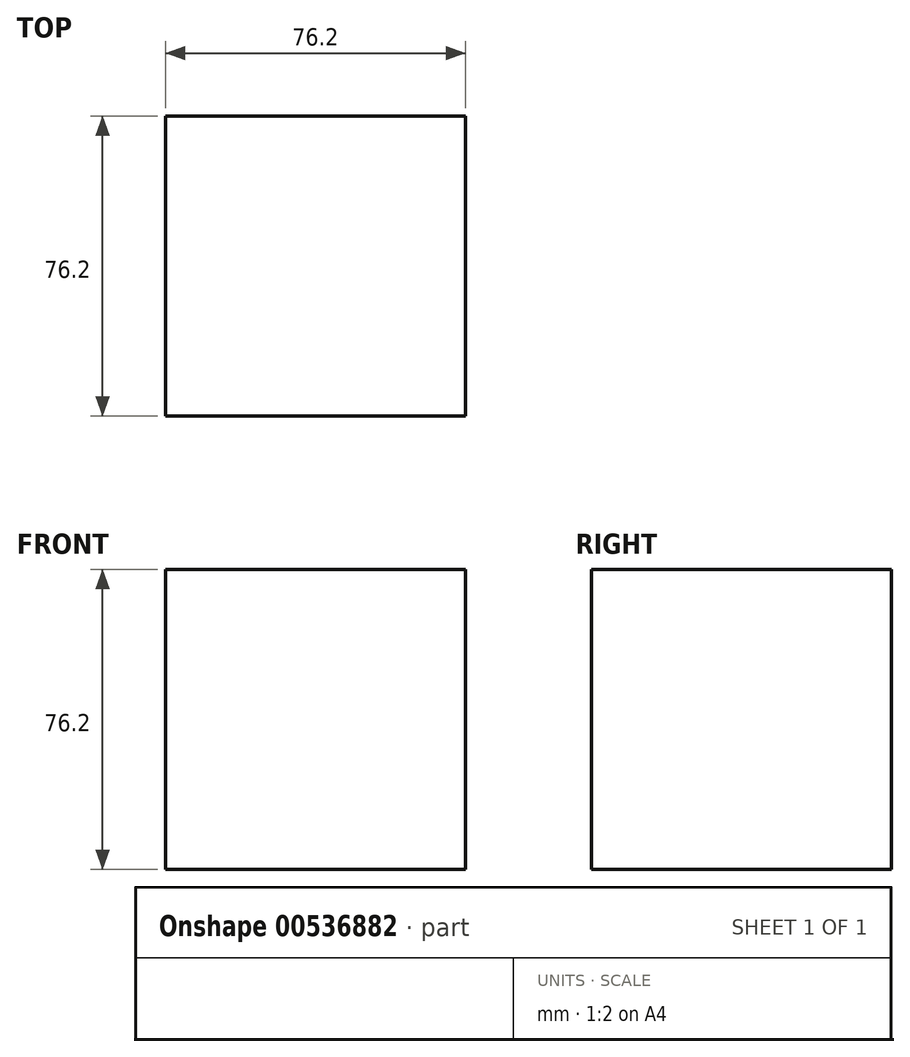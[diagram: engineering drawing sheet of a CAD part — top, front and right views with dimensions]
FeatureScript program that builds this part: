
annotation { "Feature Type Name" : "Feature", "Feature Type Description" : "" }
export const myFeature = defineFeature(function(context is Context, id is Id, definition is map)
    precondition{}
    {
        {
            var Q0;
            Q0=qCreatedBy(makeId("Front.planeOp"),FACE);
            var sketch = newSketch(context, id + "F0", { "sketchPlane" : qUnion([Q0])});
            skLineSegment(sketch, "E0.bottom", {"start": v(-32.26, 49.9) * mm, "end": v(43.94, 49.9) * mm});
            skLineSegment(sketch, "E0.top", {"start": v(-32.26, -26.3) * mm, "end": v(43.94, -26.3) * mm});
            skLineSegment(sketch, "E0.left", {"start": v(-32.26, 49.9) * mm, "end": v(-32.26, -26.3) * mm});
            skLineSegment(sketch, "E0.right", {"start": v(43.94, 49.9) * mm, "end": v(43.94, -26.3) * mm});
            skSolve(sketch);
        }
        {
            var Q0;
            Q0=makeQuery(id+"F0.imprint","IMPRINT",FACE,{"disambiguationData":[TD([[makeQuery(id+"F0.imprint","IMPRINT",EDGE,{"derivedFrom":sQuery(id+"F0.wireOp",EDGE,"E0.bottom")}),-1.0]])]});
            extrude(context, id + "F1", {"entities" : qUnion([Q0]), "depth" : 76.2 * mm, "offsetDistance" : 25.4 * mm});
        }
    });
